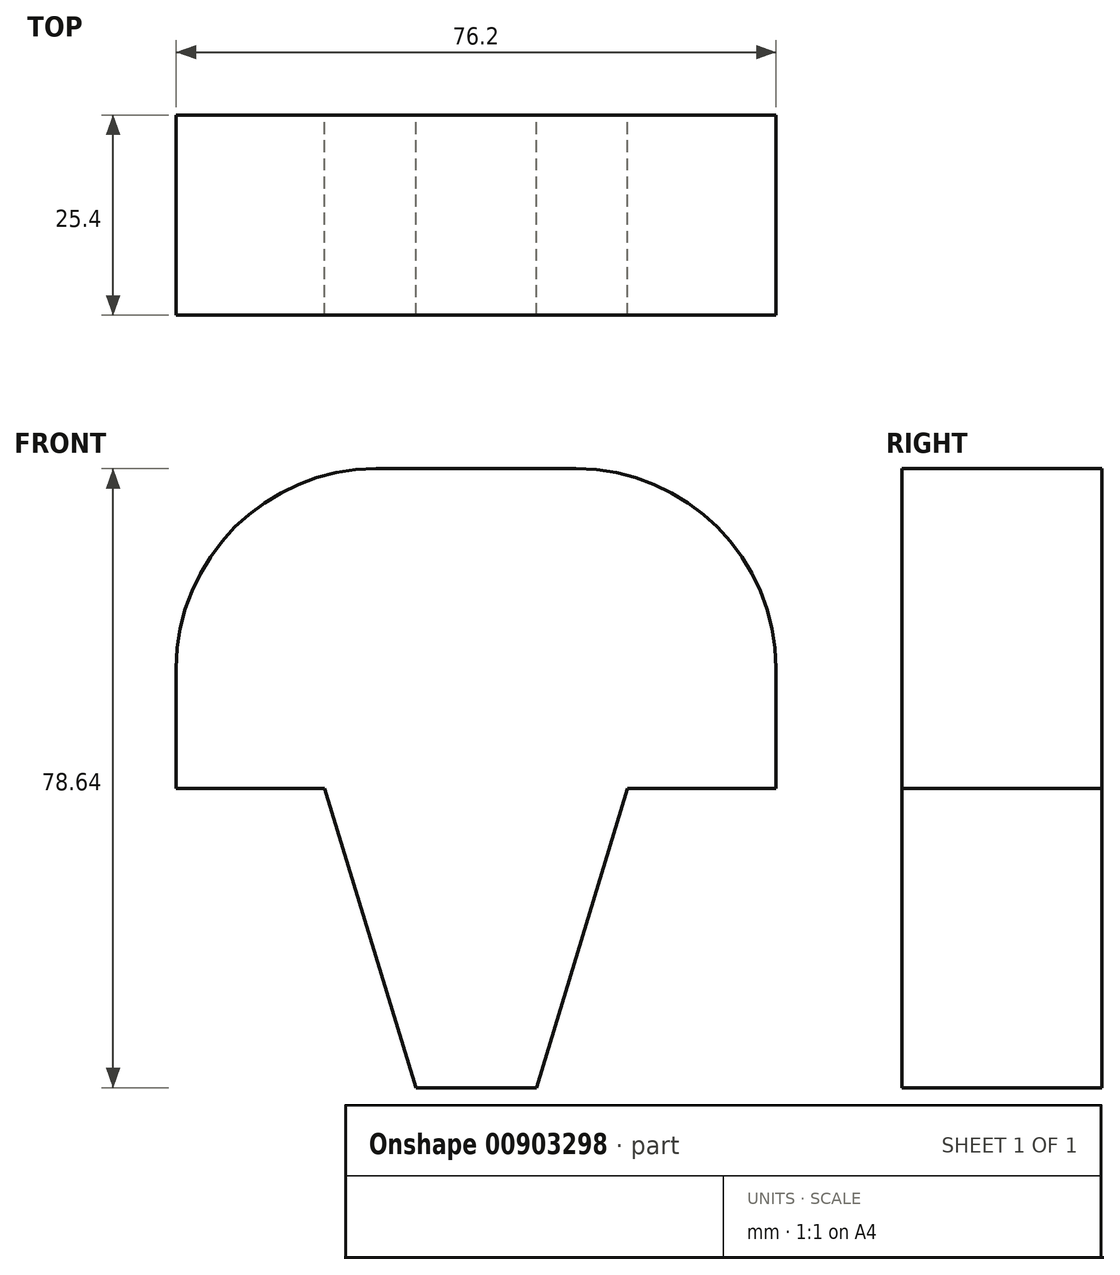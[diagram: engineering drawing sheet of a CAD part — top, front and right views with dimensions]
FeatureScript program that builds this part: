
annotation { "Feature Type Name" : "Feature", "Feature Type Description" : "" }
export const myFeature = defineFeature(function(context is Context, id is Id, definition is map)
    precondition{}
    {
        {
            var Q0;
            Q0=qCreatedBy(makeId("Front.planeOp"),FACE);
            var sketch = newSketch(context, id + "F0", { "sketchPlane" : qUnion([Q0])});
            skLineSegment(sketch, "E0.bottom", {"start": v(0, 34.43) * mm, "end": v(12.7, 34.43) * mm});
            skLineSegment(sketch, "E0.top", {"start": v(0, -6.21) * mm, "end": v(38.1, -6.21) * mm});
            skLineSegment(sketch, "E0.left", {"start": v(0, 34.43) * mm, "end": v(0, -6.21) * mm});
            skLineSegment(sketch, "E0.right", {"start": v(38.1, 9.03) * mm, "end": v(38.1, -6.21) * mm});
            skLineSegment(sketch, "E1.MirrorCS", {"start": v(-38.1, 9.03) * mm, "end": v(-38.1, -6.21) * mm});
            skLineSegment(sketch, "E2.MirrorCS", {"start": v(0, -6.21) * mm, "end": v(-38.1, -6.21) * mm});
            skLineSegment(sketch, "E3.MirrorCS", {"start": v(0, 34.43) * mm, "end": v(-12.7, 34.43) * mm});
            skPoint(sketch, "E4.visualSharp", {"position": v(-38.1, 34.43) * mm});
            skArc(sketch, "E4.filletArc", {"start": v(-12.7, 34.43) * mm, "mid": v(-30.66, 26.99) * mm, "end": v(-38.1, 9.03) * mm});
            skPoint(sketch, "E5.visualSharp", {"position": v(38.1, 34.43) * mm});
            skArc(sketch, "E5.filletArc", {"start": v(38.1, 9.03) * mm, "mid": v(30.66, 26.99) * mm, "end": v(12.7, 34.43) * mm});
            skLineSegment(sketch, "E6.bottom", {"start": v(-19.25, -6.21) * mm, "end": v(0, -5.86) * mm});
            skLineSegment(sketch, "E6.left", {"start": v(-19.25, -6.21) * mm, "end": v(-7.64, -44.21) * mm});
            skLineSegment(sketch, "E6.right", {"start": v(0, -5.86) * mm, "end": v(0, -5.86) * mm});
            skLineSegment(sketch, "E7.MirrorCS", {"start": v(19.25, -6.21) * mm, "end": v(7.64, -44.21) * mm});
            skLineSegment(sketch, "E8", {"start": v(-7.64, -44.21) * mm, "end": v(7.64, -44.21) * mm});
            skSolve(sketch);
        }
        {
            var Q0;
            Q0 = qSketchRegion(id + "F0", true);
            extrude(context, id + "F1", {"entities" : qUnion([Q0]), "depth" : 12.7 * mm, "offsetDistance" : 25.4 * mm, "hasSecondDirection" : true, "secondDirectionOppositeDirection" : true, "secondDirectionDepth" : 12.7 * mm});
        }
    });
